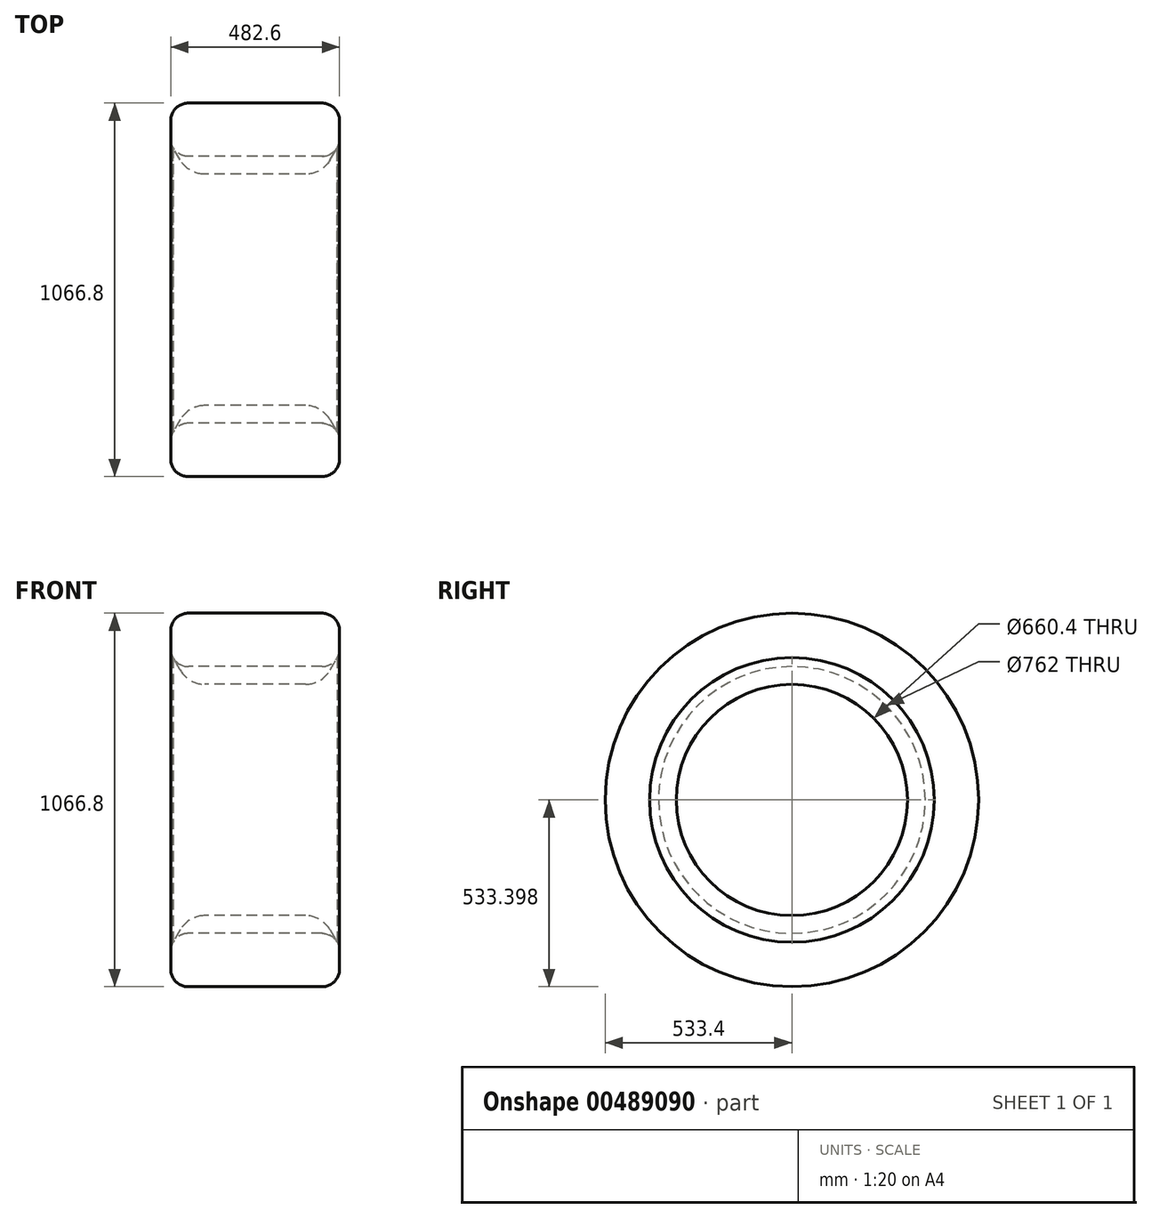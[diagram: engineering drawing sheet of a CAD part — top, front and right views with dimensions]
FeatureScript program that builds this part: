
annotation { "Feature Type Name" : "Feature", "Feature Type Description" : "" }
export const myFeature = defineFeature(function(context is Context, id is Id, definition is map)
    precondition{}
    {
        {
            var Q0;
            Q0=qCreatedBy(makeId("Front.planeOp"),FACE);
            var sketch = newSketch(context, id + "F0", { "sketchPlane" : qUnion([Q0])});
            skLineSegment(sketch, "E0.bottom", {"start": v(-11.56, 99.36) * mm, "end": v(369.44, 99.36) * mm});
            skLineSegment(sketch, "E0.top", {"start": v(-11.56, -53.04) * mm, "end": v(369.44, -53.04) * mm});
            skLineSegment(sketch, "E0.left", {"start": v(-62.36, 48.56) * mm, "end": v(-62.36, -2.24) * mm});
            skLineSegment(sketch, "E0.right", {"start": v(420.24, 48.56) * mm, "end": v(420.24, -2.24) * mm});
            skPoint(sketch, "E1.visualSharp", {"position": v(-62.36, 99.36) * mm});
            skArc(sketch, "E1.filletArc", {"start": v(-11.56, 99.36) * mm, "mid": v(-47.49, 84.48) * mm, "end": v(-62.36, 48.56) * mm});
            skPoint(sketch, "E2.visualSharp", {"position": v(420.24, 99.36) * mm});
            skArc(sketch, "E2.filletArc", {"start": v(420.24, 48.56) * mm, "mid": v(405.36, 84.48) * mm, "end": v(369.44, 99.36) * mm});
            skPoint(sketch, "E3.visualSharp", {"position": v(420.24, -53.04) * mm});
            skArc(sketch, "E3.filletArc", {"start": v(369.44, -53.04) * mm, "mid": v(405.36, -38.16) * mm, "end": v(420.24, -2.24) * mm});
            skPoint(sketch, "E4.visualSharp", {"position": v(-62.36, -53.04) * mm});
            skArc(sketch, "E4.filletArc", {"start": v(-62.36, -2.24) * mm, "mid": v(-47.49, -38.16) * mm, "end": v(-11.56, -53.04) * mm});
            skLineSegment(sketch, "E5", {"start": v(-225.1, -434.04) * mm, "end": v(488.33, -434.04) * mm});
            skSolve(sketch);
        }
        {
            var Q0;
            Q0=makeQuery(id+"F0.imprint","IMPRINT",FACE,{"disambiguationData":[TD([[makeQuery(id+"F0.imprint","IMPRINT",EDGE,{"derivedFrom":sQuery(id+"F0.wireOp",EDGE,"E0.bottom")}),-1.0]])]});
            var Q1;
            Q1=sQuery(id+"F0.wireOp",EDGE,"E5");
            revolve(context, id + "F1", {"entities" : qUnion([Q0]), "axis" : qUnion([Q1]), "revolveType" : RevolveType.FULL});
        }
        {
            var Q0;
            Q0=makeQuery(id+"F0.imprint","IMPRINT",FACE,{"disambiguationData":[TD([[makeQuery(id+"F0.imprint","IMPRINT",EDGE,{"derivedFrom":sQuery(id+"F0.wireOp",EDGE,"E0.bottom")}),-1.0]])]});
            var sketch = newSketch(context, id + "F2", { "sketchPlane" : qUnion([Q0])});
            skLineSegment(sketch, "E6", {"start": v(485.87, 97.84) * mm, "end": v(392.9, -63.2) * mm});
            skLineSegment(sketch, "E7", {"start": v(-124.66, 92.05) * mm, "end": v(-35.03, -63.2) * mm});
            skLineSegment(sketch, "E8", {"start": v(322.5, -103.84) * mm, "end": v(35.36, -103.84) * mm});
            skPoint(sketch, "E9.visualSharp", {"position": v(369.44, -103.84) * mm});
            skArc(sketch, "E9.filletArc", {"start": v(322.5, -103.84) * mm, "mid": v(363.15, -92.95) * mm, "end": v(392.9, -63.2) * mm});
            skPoint(sketch, "E10.visualSharp", {"position": v(-11.56, -103.84) * mm});
            skArc(sketch, "E10.filletArc", {"start": v(-35.03, -63.2) * mm, "mid": v(-5.28, -92.95) * mm, "end": v(35.36, -103.84) * mm});
            skSolve(sketch);
        }
        {
            var Q0;
            Q0=makeQuery(id+"F2.imprint","IMPRINT",FACE,{"disambiguationData":[TD([[makeQuery(id+"F2.imprint","IMPRINT",EDGE,{"derivedFrom":sQuery(id+"F2.wireOp",EDGE,"E8")}),-1.0]])]});
            var Q1;
            Q1=sQuery(id+"F0.wireOp",EDGE,"E5");
            revolve(context, id + "F3", {"entities" : qUnion([Q0]), "axis" : qUnion([Q1]), "revolveType" : RevolveType.FULL});
        }
    });
